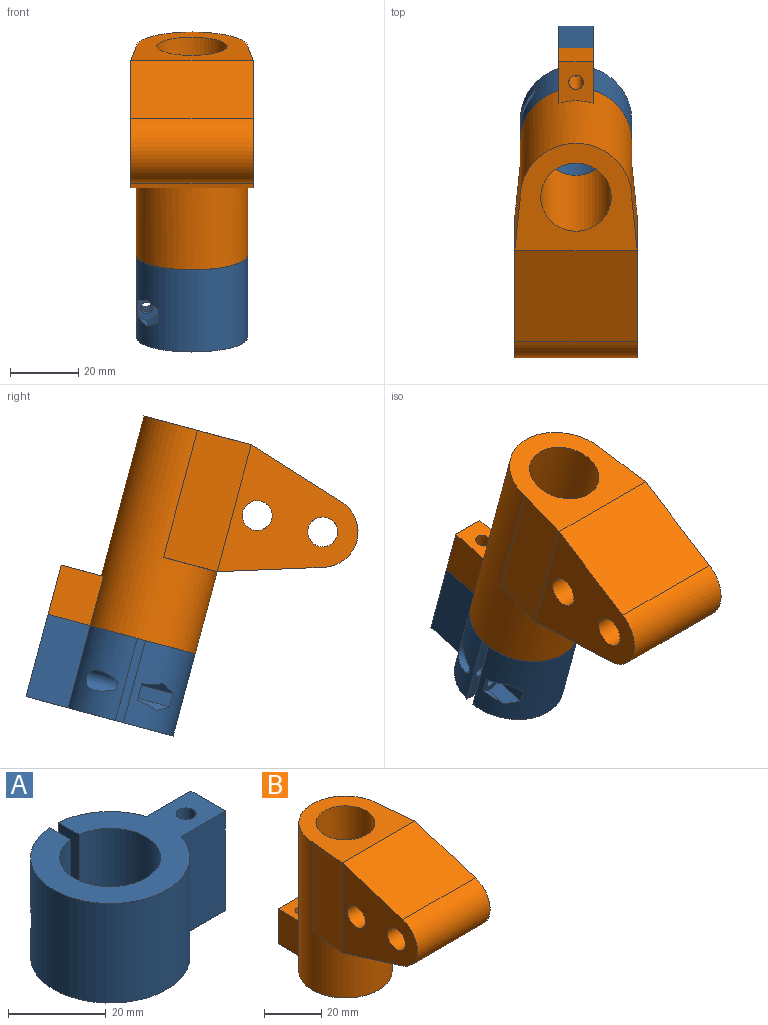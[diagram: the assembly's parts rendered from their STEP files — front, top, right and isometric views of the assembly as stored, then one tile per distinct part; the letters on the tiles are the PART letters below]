
ASSEMBLY  parts=2 mates=1
PART A: 21 faces, bbox 44.8x32.7x25 mm
  f0: cylinder r=16.35mm len=32.65mm, axis (0,0,-1), area 1695.2mm2, adj f3,f4,f9,f10,f15,f16,f17,f18
  f1: cylinder r=1.75mm len=3.5mm, axis (-1,0,0), area 24mm2, adj f7,f14
  f2: cylinder r=16.35mm len=25mm, axis (0,0,-1), area 430.7mm2, adj f6,f7,f9,f10,f13,f14
  f3: plane 25x6.03mm, normal (1,0,0), area 141.1mm2, adj f0,f8,f9,f10,f11
  f4: plane 25x12.86mm, normal (0,-1,0), area 321.6mm2, adj f0,f5,f9,f10
  f5: plane 25x10mm, normal (1,0,0), area 250mm2, adj f4,f6,f9,f10
  f6: plane 25x12.86mm, normal (0,1,0), area 321.6mm2, adj f2,f5,f9,f10
  f7: plane 25x6.03mm, normal (-1,0,0), area 141.1mm2, adj f1,f2,f8,f9,f10
  f8: cylinder r=10.35mm len=25mm, axis (0,0,-1), area 1563.1mm2, adj f3,f7,f9,f10
  f9: plane 44.78x32.65mm, normal (0,0,1), area 598.4mm2, adj f0,f2,f3,f4,f5,f6,f7,f8
  f10: plane 44.78x32.65mm, normal (0,0,-1), area 598.4mm2, adj f0,f2,f3,f4,f5,f6,f7,f8
  f11: cylinder r=1.75mm len=3.5mm, axis (1,0,0), area 24.7mm2, adj f3,f20
  f12: cylinder r=2.05mm len=25mm, axis (0,0,-1), area 322mm2, adj f9,f10
  f13: cylinder r=3mm len=9.29mm, axis (1,0,0), area 99.7mm2, adj f2,f14
  f14: plane 6x5.71mm, normal (1,0,0), area 18.2mm2, adj f1,f2,f13
  f15: plane 9.58x4.04mm, normal (0,1,0), area 38.7mm2, adj f0,f16,f19,f20
  f16: plane 9.58x3.5mm, normal (0,0.5,0.86), area 32.2mm2, adj f0,f15,f17,f20
  f17: plane 6x2.67mm, normal (0,-0.5,0.87), area 10.9mm2, adj f0,f16,f20
  f18: plane 5.98x2.65mm, normal (0,-0.5,-0.86), area 10.8mm2, adj f0,f19,f20
  f19: plane 9.57x3.51mm, normal (0,0.5,-0.87), area 32.2mm2, adj f0,f15,f18,f20
  f20: plane 8.08x6.16mm, normal (-1,0,0), area 29mm2, adj f0,f11,f15,f16,f17,f18,f19
PART B: 20 faces, bbox 36x82.1x63.6 mm
  f0: cylinder r=2.15mm len=15mm, axis (0,0,1), area 202.6mm2, adj f15,f19
  f1: cylinder r=16.35mm len=63.6mm, axis (0,0,-1), area 4398.5mm2, adj f2,f3,f6,f7,f8,f15,f16,f17
  f2: plane 18x16.35mm, normal (0,0,-1), area 70.9mm2, adj f1,f8,f14
  f3: plane 18x16.35mm, normal (0,0,-1), area 70.9mm2, adj f1,f7,f14
  f4: plane 38.6x37.3mm, normal (1,0,0), area 861.6mm2, adj f7,f10,f11,f12,f13,f14
  f5: plane 38.6x37.3mm, normal (-1,0,0), area 861.6mm2, adj f8,f10,f11,f12,f13,f14
  f6: plane 36x32.7mm, normal (0,0,1), area 645mm2, adj f1,f7,f8,f9,f10
  f7: plane 38.6x16.35mm, normal (0.99,0.1,0), area 634.3mm2, adj f1,f3,f4,f6
  f8: plane 38.6x16.35mm, normal (-0.99,0.1,0), area 634.3mm2, adj f1,f2,f5,f6
  f9: cylinder r=10.35mm len=63.6mm, axis (0,0,-1), area 4136mm2, adj f6,f15
  f10: plane 36x30mm, normal (0,-0.3,0.95), area 1131.5mm2, adj f4,f5,f6,f11
  f11: cylinder r=10.4mm len=36mm, axis (1,0,0), area 949.5mm2, adj f4,f5,f10,f14
  f12: cylinder r=4.4mm len=36mm, axis (1,0,0), area 995.3mm2, adj f4,f5
  f13: cylinder r=4.4mm len=36mm, axis (1,0,0), area 995.3mm2, adj f4,f5
  f14: plane 36x30mm, normal (0,-0.3,-0.95), area 1131.5mm2, adj f2,f3,f4,f5,f11
  f15: plane 44.78x32.7mm, normal (0,0,-1), area 612.2mm2, adj f0,f1,f9,f16,f17,f18
  f16: plane 15x12.87mm, normal (-1,0,0), area 193mm2, adj f1,f15,f18,f19
  f17: plane 15x12.87mm, normal (1,0,0), area 193mm2, adj f1,f15,f18,f19
  f18: plane 15x10mm, normal (0,1,0), area 150mm2, adj f15,f16,f17,f19
  f19: plane 12.87x10mm, normal (0,0,1), area 108.9mm2, adj f0,f1,f16,f17,f18
PLACE A rot(axis=(0.13,-0.13,0.98),91deg) t=(-19.39,19.84,-32.69)mm
PLACE B rot(axis=(1,0,0),15deg) t=(-19.39,-11.11,10.78)mm
MATE revolute B.f9 <-> A.f8  axis (0,0.26,-0.97) through (-19.39,13.37,-8.54)mm
